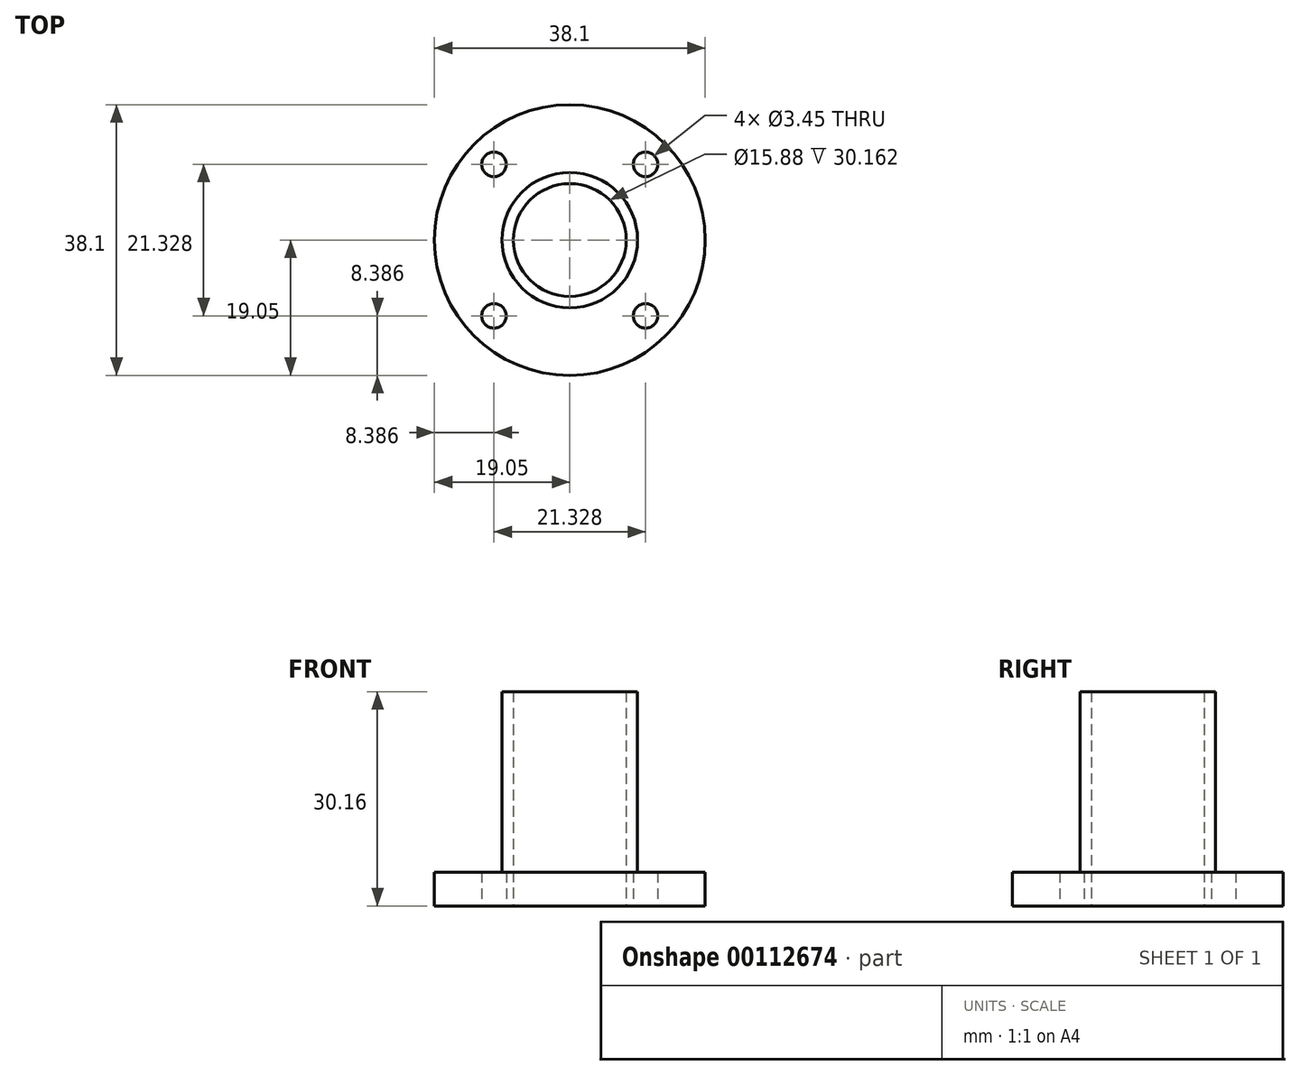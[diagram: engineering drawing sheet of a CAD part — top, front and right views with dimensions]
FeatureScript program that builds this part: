
annotation { "Feature Type Name" : "Feature", "Feature Type Description" : "" }
export const myFeature = defineFeature(function(context is Context, id is Id, definition is map)
    precondition{}
    {
        {
            var Q0;
            Q0=qCreatedBy(makeId("Top.planeOp"),FACE);
            var sketch = newSketch(context, id + "F0", { "sketchPlane" : qUnion([Q0])});
            skCircle(sketch, "E0", {"center": v(0, 0) * mm, "radius": 19.05 * mm});
            skLineSegment(sketch, "E1.bottom", {"start": v(10.66, 10.66) * mm, "end": v(-10.66, 10.66) * mm, "construction": true});
            skLineSegment(sketch, "E1.top", {"start": v(10.66, -10.66) * mm, "end": v(-10.66, -10.66) * mm, "construction": true});
            skLineSegment(sketch, "E1.left", {"start": v(10.66, 10.66) * mm, "end": v(10.66, -10.66) * mm, "construction": true});
            skLineSegment(sketch, "E1.right", {"start": v(-10.66, 10.66) * mm, "end": v(-10.66, -10.66) * mm, "construction": true});
            skCircle(sketch, "E2", {"center": v(-10.66, 10.66) * mm, "radius": 1.73 * mm});
            skCircle(sketch, "E3", {"center": v(-10.66, -10.66) * mm, "radius": 1.73 * mm});
            skCircle(sketch, "E4", {"center": v(10.66, -10.66) * mm, "radius": 1.73 * mm});
            skCircle(sketch, "E5", {"center": v(10.66, 10.66) * mm, "radius": 1.73 * mm});
            skCircle(sketch, "E6", {"center": v(-10.66, 10.66) * mm, "radius": 3.97 * mm, "construction": true});
            skCircle(sketch, "E7", {"center": v(0, 0) * mm, "radius": 7.94 * mm});
            skSolve(sketch);
        }
        {
            var Q0;
            Q0 = qSketchRegion(id + "F0", true);
            extrude(context, id + "F1", {"entities" : qUnion([Q0]), "depth" : 4.76 * mm});
        }
        {
            var Q0;
            Q0=makeQuery(id+"F1.opExtrude","CAP_FACE",FACE,{"disambiguationData":[OSD([sQuery(id+"F0.wireOp",EDGE,"E0"),sQuery(id+"F0.wireOp",EDGE,"E2"),sQuery(id+"F0.wireOp",EDGE,"E3"),sQuery(id+"F0.wireOp",EDGE,"E4"),sQuery(id+"F0.wireOp",EDGE,"E5")])],"isStart":false});
            var sketch = newSketch(context, id + "F2", { "sketchPlane" : qUnion([Q0])});
            skSolve(sketch);
        }
        {
            var Q0;
            Q0=makeQuery(id+"F2.imprint","IMPRINT",FACE,{"disambiguationData":[TD([[makeQuery(id+"F2.imprint","IMPRINT",EDGE,{"derivedFrom":makeQuery(id+"F1.opExtrude","CAP_EDGE",EDGE,{"disambiguationData":[OSD([sQuery(id+"F0.wireOp",EDGE,"E0")])],"isStart":false})}),1.0]])]});
            var sketch = newSketch(context, id + "F3", { "sketchPlane" : qUnion([Q0])});
            skCircle(sketch, "E8", {"center": v(0, 0) * mm, "radius": 9.53 * mm});
            skCircle(sketch, "E9", {"center": v(0, 0) * mm, "radius": 7.94 * mm});
            skSolve(sketch);
        }
        {
            var Q0;
            Q0 = qSketchRegion(id + "F3", true);
            extrude(context, id + "F4", {"entities" : qUnion([Q0]), "operationType" : NewBodyOperationType.ADD, "depth" : 25.4 * mm});
        }
    });
